# Revit family: РИДАН_Датчик температуры MBT5250R
name_source: partatom
category: Арматура трубопроводов
units: mm (PartAtom-declared; Revit-internal decimal feet)

## family parameters
Всегда вертикально = Да
На основе рабочей плоскости = Нет
Общий = Нет
При загрузке вырезать с полостями = Нет
Размер круглого соединителя = Использовать диаметр
Тип детали = Нормальный

## types (10) — shared parameters
ADSK_Версия Revit = 2019
ADSK_Версия семейства = 1.0
ADSK_Единица измерения = шт.
ADSK_Завод-изготовитель = ООО «Ридан-Трейд»
ADSK_Количество = 1
ADSK_Марка = MBT5250R
zero-valued in all types: ADSK_Масса

## per-type parameters (varying)
| type | ADSK_Код изделия | ADSK_Наименование | L | a | Гильза_ |
| MBT5250 RPt1000 L=50мм | 084Z8083R | Термопреобразователь сопротивления (датчик температуры) MBT5250R Pt1000 L=50 мм | 35 мм | 50 мм | Влж_Гильза для MBT5250R : Гильза для MBT5250R L=50мм |
| MBT5250 RPt1000 L=100мм | 084Z8139R | Термопреобразователь сопротивления (датчик температуры) MBT5250R Pt1000 L=100 мм | 85 мм | 100 мм | Влж_Гильза для MBT5250R : Гильза для MBT5250R L=100мм |
| MBT5250 RPt1000 L=150мм | 084Z2113R | Термопреобразователь сопротивления (датчик температуры) MBT5250R Pt1000 L=150 мм | 135 мм | 150 мм | Влж_Гильза для MBT5250R : Гильза для MBT5250R L=150мм |
| MBT5250 RPt1000 L=200мм | 084Z2257R | Термопреобразователь сопротивления (датчик температуры) MBT5250R Pt1000 L=200 мм | 185 мм | 200 мм | Влж_Гильза для MBT5250R : Гильза для MBT5250R L=200мм |
| MBT5250 RPt1000 L=250мм | 084Z2258R | Термопреобразователь сопротивления (датчик температуры) MBT5250R Pt1000 L=250 мм | 235 мм | 250 мм | Влж_Гильза для MBT5250R : Гильза для MBT5250R L=250мм |
| MBT5250 RPt100 L=50мм | 084Z8011R | Термопреобразователь сопротивления (датчик температуры) MBT5250R Pt100 L=50 мм | 35 мм | 50 мм | Влж_Гильза для MBT5250R : Гильза для MBT5250R L=50мм |
| MBT5250 RPt100 L=100мм | 084Z8012R | Термопреобразователь сопротивления (датчик температуры) MBT5250R Pt100 L=100 мм | 85 мм | 100 мм | Влж_Гильза для MBT5250R : Гильза для MBT5250R L=100мм |
| MBT5250 RPt100 L=150мм | 084Z8010R | Термопреобразователь сопротивления (датчик температуры) MBT5250R Pt100 L=150 мм | 135 мм | 150 мм | Влж_Гильза для MBT5250R : Гильза для MBT5250R L=150мм |
| MBT5250 RPt100 L=200мм | 084Z8022R | Термопреобразователь сопротивления (датчик температуры) MBT5250R Pt100 L=200 мм | 185 мм | 200 мм | Влж_Гильза для MBT5250R : Гильза для MBT5250R L=200мм |
| MBT5250 RPt100 L=250мм | 084Z8023R | Термопреобразователь сопротивления (датчик температуры) MBT5250R Pt100 L=250 мм | 235 мм | 250 мм | Влж_Гильза для MBT5250R : Гильза для MBT5250R L=250мм |
